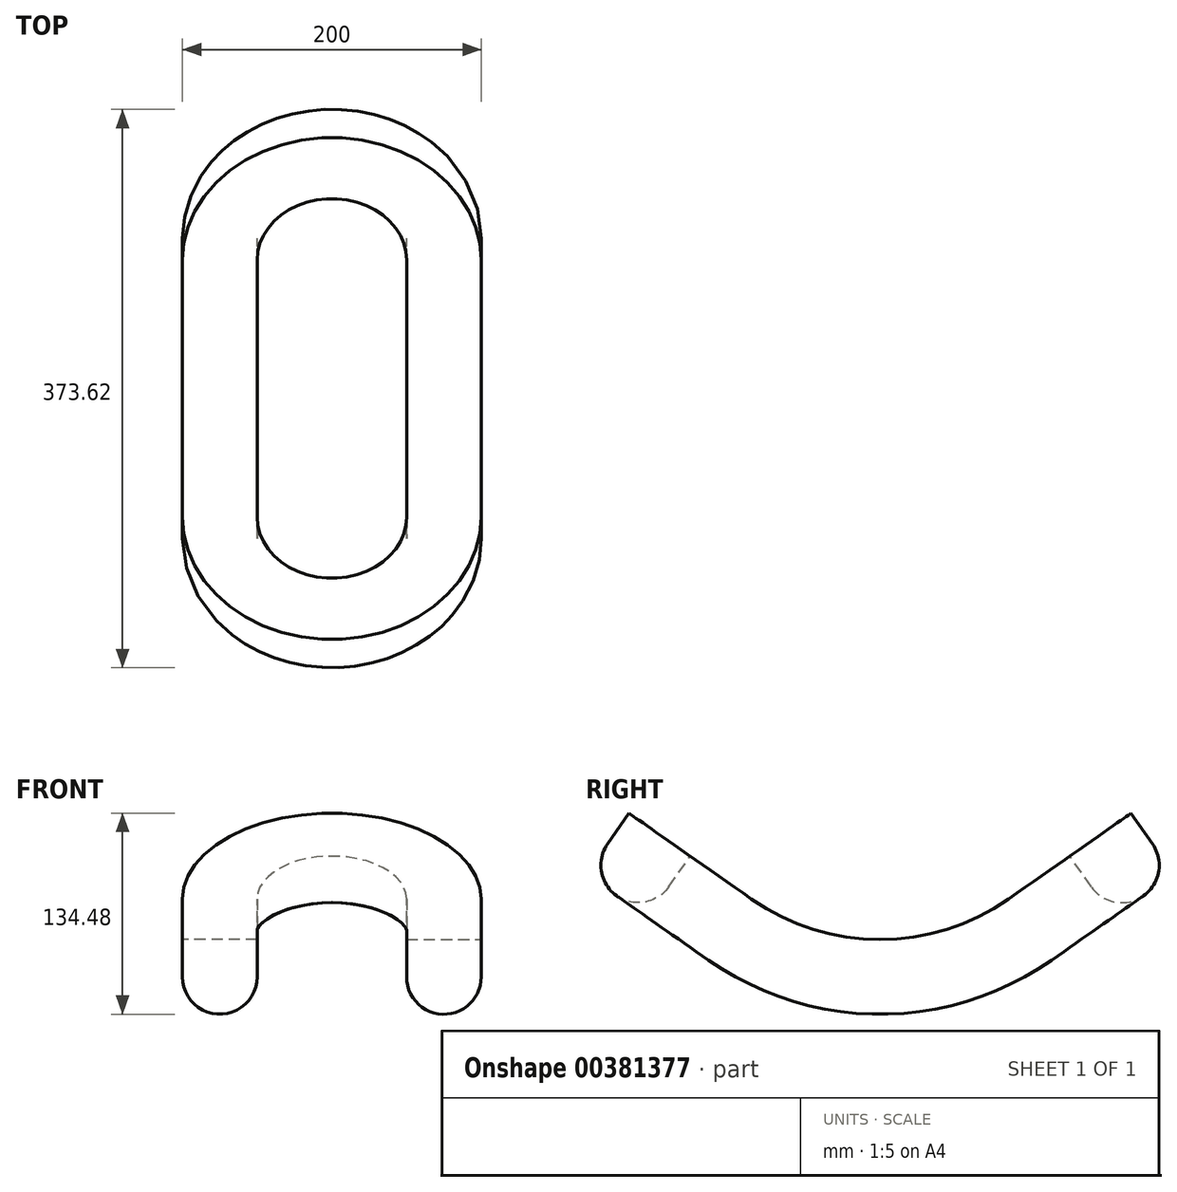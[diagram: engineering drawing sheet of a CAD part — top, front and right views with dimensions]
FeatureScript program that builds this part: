
annotation { "Feature Type Name" : "Feature", "Feature Type Description" : "" }
export const myFeature = defineFeature(function(context is Context, id is Id, definition is map)
    precondition{}
    {
        {
            var Q0;
            Q0=qCreatedBy(makeId("Right.planeOp"),FACE);
            var sketch = newSketch(context, id + "F0", { "sketchPlane" : qUnion([Q0])});
            skArc(sketch, "E0", {"start": v(0, 0) * mm, "mid": v(45.1, 6.94) * mm, "end": v(86.04, 27.13) * mm});
            skLineSegment(sketch, "E1", {"start": v(86.04, 27.13) * mm, "end": v(167.95, 84.48) * mm});
            skLineSegment(sketch, "E2", {"start": v(86.04, 27.13) * mm, "end": v(0, 150) * mm, "construction": true});
            skLineSegment(sketch, "E3", {"start": v(0, 150) * mm, "end": v(0, 0) * mm, "construction": true});
            skSolve(sketch);
        }
        {
            var Q0;
            Q0=sQuery(id+"F0.wireOp",EDGE,"E1");
            var Q1;
            Q1=sQuery(id+"F0.wireOp",EDGE,"E0");
            extrude(context, id + "F1", {"bodyType" : ToolBodyType.SURFACE, "surfaceEntities" : qUnion([Q0, Q1]), "depth" : 100 * mm});
        }
        {
            var Q0;
            Q0=qCreatedBy(makeId("Front.planeOp"),FACE);
            var sketch = newSketch(context, id + "F2", { "sketchPlane" : qUnion([Q0])});
            skLineSegment(sketch, "E4.bottom", {"start": v(100, 0) * mm, "end": v(50, 0) * mm});
            skLineSegment(sketch, "E4.top", {"start": v(100, -25) * mm, "end": v(50, -25) * mm});
            skLineSegment(sketch, "E4.left", {"start": v(100, 0) * mm, "end": v(100, -25) * mm});
            skLineSegment(sketch, "E4.right", {"start": v(50, 0) * mm, "end": v(50, -25) * mm});
            skArc(sketch, "E5", {"start": v(100, -25) * mm, "mid": v(75, -50) * mm, "end": v(50, -25) * mm});
            skSolve(sketch);
        }
        {
            var Q0;
            Q0=makeQuery(id+"F1.opExtrude","SWEPT_FACE",FACE,{"disambiguationData":[OSD([sQuery(id+"F0.wireOp",EDGE,"E1")])]});
            var sketch = newSketch(context, id + "F3", { "sketchPlane" : qUnion([Q0])});
            skLineSegment(sketch, "E6", {"start": v(0, -86.04) * mm, "end": v(100, -86.04) * mm});
            skArc(sketch, "E7", {"start": v(100, -86.04) * mm, "mid": v(70.71, -156.75) * mm, "end": v(0, -186.04) * mm});
            skSolve(sketch);
        }
        {
            var Q0;
            Q0=makeQuery(id+"F2.imprint","IMPRINT",FACE,{"disambiguationData":[TD([[makeQuery(id+"F2.imprint","IMPRINT",EDGE,{"derivedFrom":sQuery(id+"F2.wireOp",EDGE,"E4.bottom")}),1.0]])]});
            var Q1;
            Q1=makeQuery(id+"F2.imprint","IMPRINT",FACE,{"disambiguationData":[TD([[makeQuery(id+"F2.imprint","IMPRINT",EDGE,{"derivedFrom":sQuery(id+"F2.wireOp",EDGE,"E4.top")}),1.0]])]});
            var Q2;
            Q2=makeQuery(id+"F1.opExtrude","CAP_EDGE",EDGE,{"disambiguationData":[OSD([sQuery(id+"F0.wireOp",EDGE,"E0")])],"isStart":false});
            var Q3;
            Q3=sQuery(id+"F3.wireOp",EDGE,"E7");
            sweep(context, id + "F4", {"profiles" : qUnion([Q0, Q1]), "path" : qUnion([Q2, Q3])});
        }
        {
            var Q0;
            Q0=makeQuery(id+"F4.opSweep","SWEPT_BODY",BODY,{"disambiguationData":[OSD([sQuery(id+"F2.wireOp",EDGE,"E4.bottom"),sQuery(id+"F2.wireOp",EDGE,"E4.left"),sQuery(id+"F2.wireOp",EDGE,"E4.right"),sQuery(id+"F2.wireOp",EDGE,"E5"),sQuery(id+"F3.wireOp",EDGE,"E7")])]});
            var Q1;
            Q1=qCreatedBy(makeId("Right.planeOp"),FACE);
            mirror(context, id + "F5", {"operationType" : NewBodyOperationType.ADD, "entities" : qUnion([Q0]), "mirrorPlane" : qUnion([Q1])});
        }
        {
            var Q0;
            Q0=makeQuery(id+"F4.opSweep","SWEPT_BODY",BODY,{"disambiguationData":[OSD([sQuery(id+"F2.wireOp",EDGE,"E4.bottom"),sQuery(id+"F2.wireOp",EDGE,"E4.left"),sQuery(id+"F2.wireOp",EDGE,"E4.right"),sQuery(id+"F2.wireOp",EDGE,"E5"),sQuery(id+"F3.wireOp",EDGE,"E7")])]});
            var Q1;
            Q1=qCreatedBy(makeId("Front.planeOp"),FACE);
            mirror(context, id + "F6", {"operationType" : NewBodyOperationType.ADD, "entities" : qUnion([Q0]), "mirrorPlane" : qUnion([Q1])});
        }
    });
